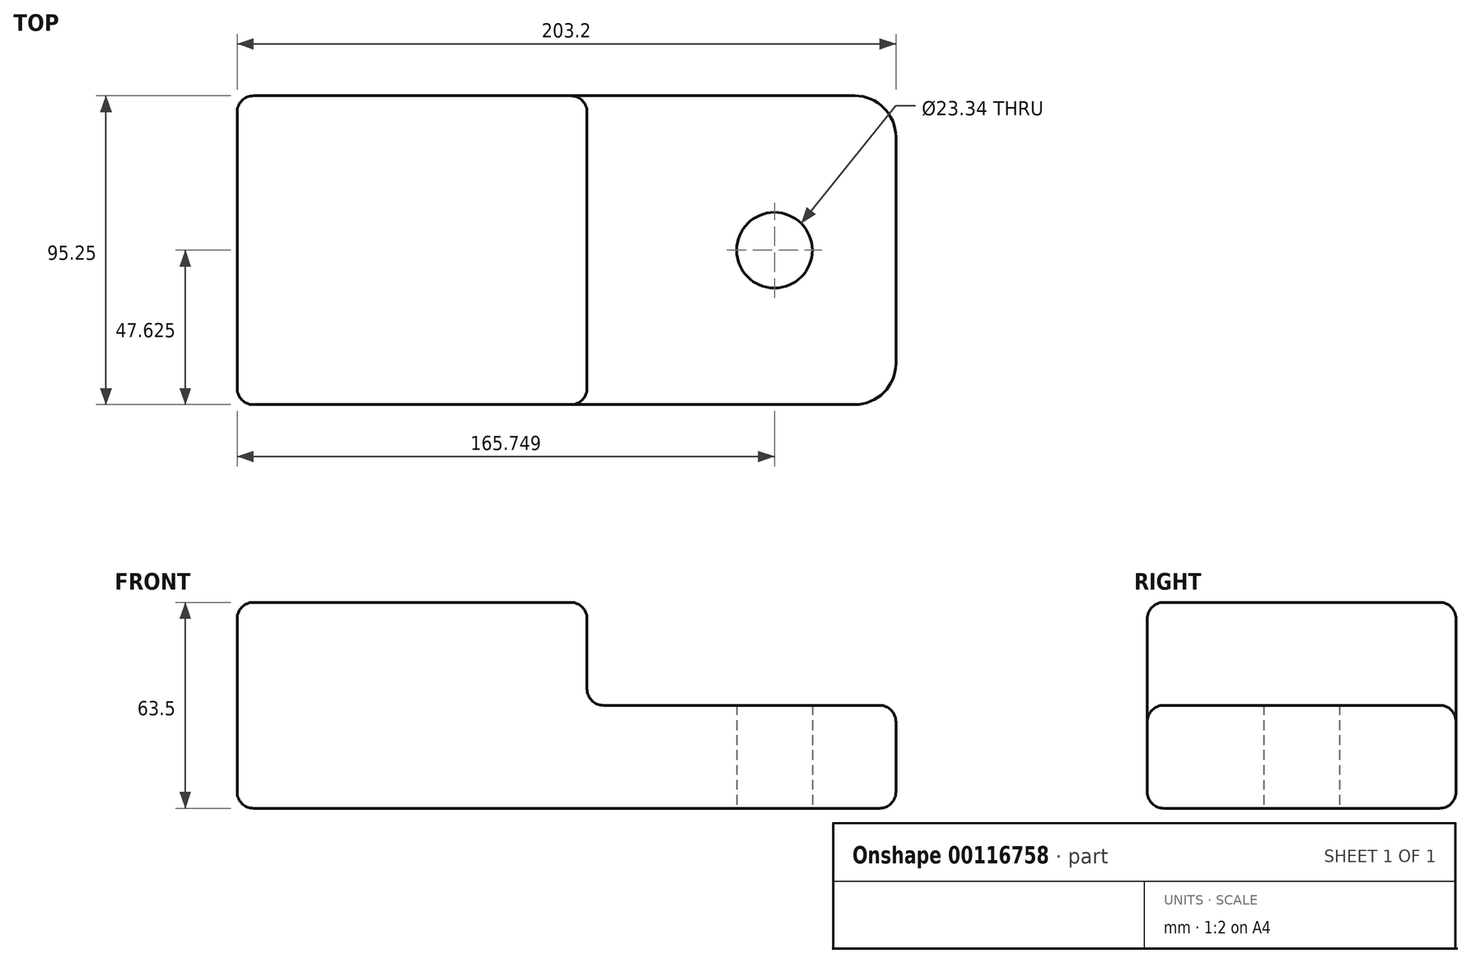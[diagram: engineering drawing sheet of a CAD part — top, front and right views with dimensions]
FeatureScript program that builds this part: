
annotation { "Feature Type Name" : "Feature", "Feature Type Description" : "" }
export const myFeature = defineFeature(function(context is Context, id is Id, definition is map)
    precondition{}
    {
        {
            var Q0;
            Q0=qCreatedBy(makeId("Top.planeOp"),FACE);
            var sketch = newSketch(context, id + "F0", { "sketchPlane" : qUnion([Q0])});
            skLineSegment(sketch, "E0.bottom", {"start": v(-203.2, 95.25) * mm, "end": v(-12.7, 95.25) * mm});
            skLineSegment(sketch, "E0.top", {"start": v(-203.2, 0) * mm, "end": v(-12.7, 0) * mm});
            skLineSegment(sketch, "E0.left", {"start": v(-203.2, 95.25) * mm, "end": v(-203.2, 0) * mm});
            skLineSegment(sketch, "E0.right", {"start": v(0, 82.55) * mm, "end": v(0, 12.7) * mm});
            skLineSegment(sketch, "E1", {"start": v(-95.25, 95.25) * mm, "end": v(-95.25, 0) * mm});
            skCircle(sketch, "E2", {"center": v(-37.45, 47.62) * mm, "radius": 11.67 * mm});
            skPoint(sketch, "E2.centerSnap0", {"position": v(0, 47.62) * mm});
            skPoint(sketch, "E3.visualSharp", {"position": v(0, 95.25) * mm});
            skArc(sketch, "E3.filletArc", {"start": v(0, 82.55) * mm, "mid": v(-3.72, 91.53) * mm, "end": v(-12.7, 95.25) * mm});
            skPoint(sketch, "E4.visualSharp", {"position": v(0, 0) * mm});
            skArc(sketch, "E4.filletArc", {"start": v(-12.7, 0) * mm, "mid": v(-3.72, 3.72) * mm, "end": v(0, 12.7) * mm});
            skSolve(sketch);
        }
        {
            var Q0;
            {var subQ0=sQuery(id+"F0.wireOp",EDGE,"E0.left");Q0=makeQuery(id+"F0.imprint","IMPRINT",FACE,{"disambiguationData":[TD([[makeQuery(id+"F0.imprint","IMPRINT",EDGE,{"derivedFrom":subQ0}),1.0]])]});}
            extrude(context, id + "F1", {"entities" : qUnion([Q0]), "depth" : 63.5 * mm});
        }
        {
            var Q0;
            Q0=makeQuery(id+"F0.imprint","IMPRINT",FACE,{"disambiguationData":[TD([[makeQuery(id+"F0.imprint","IMPRINT",EDGE,{"derivedFrom":sQuery(id+"F0.wireOp",EDGE,"E0.right")}),-1.0]])]});
            extrude(context, id + "F2", {"entities" : qUnion([Q0]), "operationType" : NewBodyOperationType.ADD, "depth" : 25.4 * mm});
        }
        {
            var Q0;
            Q0=makeQuery(id+"F2.opExtrude","CAP_FACE",FACE,{"disambiguationData":[OSD([sQuery(id+"F0.wireOp",EDGE,"E0.bottom"),sQuery(id+"F0.wireOp",EDGE,"E0.top"),sQuery(id+"F0.wireOp",EDGE,"E0.right"),sQuery(id+"F0.wireOp",EDGE,"E1"),sQuery(id+"F0.wireOp",EDGE,"E2"),sQuery(id+"F0.wireOp",EDGE,"E3.filletArc"),sQuery(id+"F0.wireOp",EDGE,"E4.filletArc")])],"isStart":false});
            extrude(context, id + "F3", {"entities" : qUnion([Q0]), "operationType" : NewBodyOperationType.ADD, "depth" : 6.35 * mm});
        }
        {
            var Q0;
            {var subQ0=sQuery(id+"F0.wireOp",EDGE,"E0.right");Q0=makeQuery(id+"F3.boolean.opBoolean","MERGE",FACE,{"derivedFrom":[makeQuery(id+"F2.opExtrude","SWEPT_FACE",FACE,{"disambiguationData":[OSD([subQ0])]}),makeQuery(id+"F3.opExtrude","SWEPT_FACE",FACE,{"disambiguationData":[OSD([subQ0])]})]});}
            var Q1;
            Q1=makeQuery(id+"F1.opExtrude","SWEPT_FACE",FACE,{"disambiguationData":[OSD([sQuery(id+"F0.wireOp",EDGE,"E1")])]});
            var Q2;
            Q2=makeQuery(id+"F1.opExtrude","CAP_FACE",FACE,{"disambiguationData":[OSD([sQuery(id+"F0.wireOp",EDGE,"E0.bottom"),sQuery(id+"F0.wireOp",EDGE,"E0.top"),sQuery(id+"F0.wireOp",EDGE,"E0.left"),sQuery(id+"F0.wireOp",EDGE,"E1")])],"isStart":false});
            var Q3;
            Q3=makeQuery(id+"F1.opExtrude","SWEPT_FACE",FACE,{"disambiguationData":[OSD([sQuery(id+"F0.wireOp",EDGE,"E0.left")])]});
            fillet(context, id + "F4", {"entities" : qUnion([Q0, Q1, Q2, Q3]), "radius" : 5.08 * mm, "tangentPropagation" : true, "allowEdgeOverflow" : false});
        }
    });
